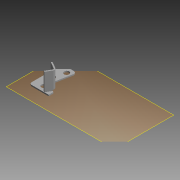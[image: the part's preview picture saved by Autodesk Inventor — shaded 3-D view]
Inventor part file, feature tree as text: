
AUTODESK INVENTOR PART (.ipt)
format: ipt  version: 2015 (Build 190159000, 159)  size: 165,376 bytes
history: native  units: mm
features: sheet_metal_op x10, reference x7, sketch x4, other x4, plane x1, hole x1
ambient origin geometry x8: Origin, YZ Plane, XZ Plane, XY Plane, X Axis, Y Axis, Z Axis, Center Point
bodies: Solid1 (feature_tree)
feature tree (27):
  plane  "Work Plane1"
  sheet_metal_op  "Face1"
  sheet_metal_op  "Flange1"
  sheet_metal_op  "Flange2"
  sheet_metal_op  "Flange3"
  hole  "Hole1"  [1 undecoded]
  sketch  "Sketch1"  dims[d0=2.0mm d1=2.0mm]
  reference  "Reference1"
  reference  "Reference2"
  reference  "Reference3"
  reference  "Reference4"
  reference  "Reference5"
  reference  "Reference6"
  reference  "Reference7"
  other  "Plate1"
  sketch  "Sketch2"  dims[d2=1.0mm]
  other  "Plate2"
  sheet_metal_op  "Bend1"
  sheet_metal_op  "Corner1"
  sketch  "Sketch3"  dims[d3=1.0mm]
  other  "Plate3"
  sheet_metal_op  "Bend2"
  sheet_metal_op  "Corner2"
  sketch  "Sketch4"  dims[d4=0.5mm d5=2.0mm d6=1.0mm d7=15.0mm d8=90.0deg d9=1.0mm d10=4.0mm d11=1.0mm d12=1.0mm d13=1.0mm d14=0.5mm d15=2.0mm d16=1.0mm d17=7.0mm d18=90.0deg d19=1.0mm d20=4.0mm d21=1.0mm d22=1.0mm d23=1.0mm d24=0.5mm d25=2.0mm d26=1.0mm d27=1.0mm d28=0.0mm d29=1.0mm d30=4.0mm d31=1.0mm d32=1.0mm d33=4.0mm d34=4.0mm d35=3.0mm d36=6.0mm d37=4.0mm d38=2.0mm d39=90.0deg d40=1.0mm d41=20.594885mm]
  other  "Plate4"
  sheet_metal_op  "Bend3"
  sheet_metal_op  "Corner3"
note: 1 required parameter value undecoded (feature->parameter linkage not recoverable at this tier; creation-order binding heuristic only, values carry confidence <= 0.55)
